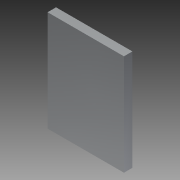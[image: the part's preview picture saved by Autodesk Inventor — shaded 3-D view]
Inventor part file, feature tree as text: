
AUTODESK INVENTOR PART (.ipt)
format: ipt  version: 2015 (Build 190159000, 159)  size: 75,776 bytes
history: native  units: mm
features: extrude x1, sketch x1
ambient origin geometry x8: Origin, YZ Plane, XZ Plane, XY Plane, X Axis, Y Axis, Z Axis, Center Point
bodies: Solid1 (feature_tree)
feature tree (2):
  extrude  "Extrusion1"  Depth=95.0mm
  sketch  "Sketch1"  dims[d0=72.0mm d1=95.0mm d2=8.0mm d3=0.0mm]
